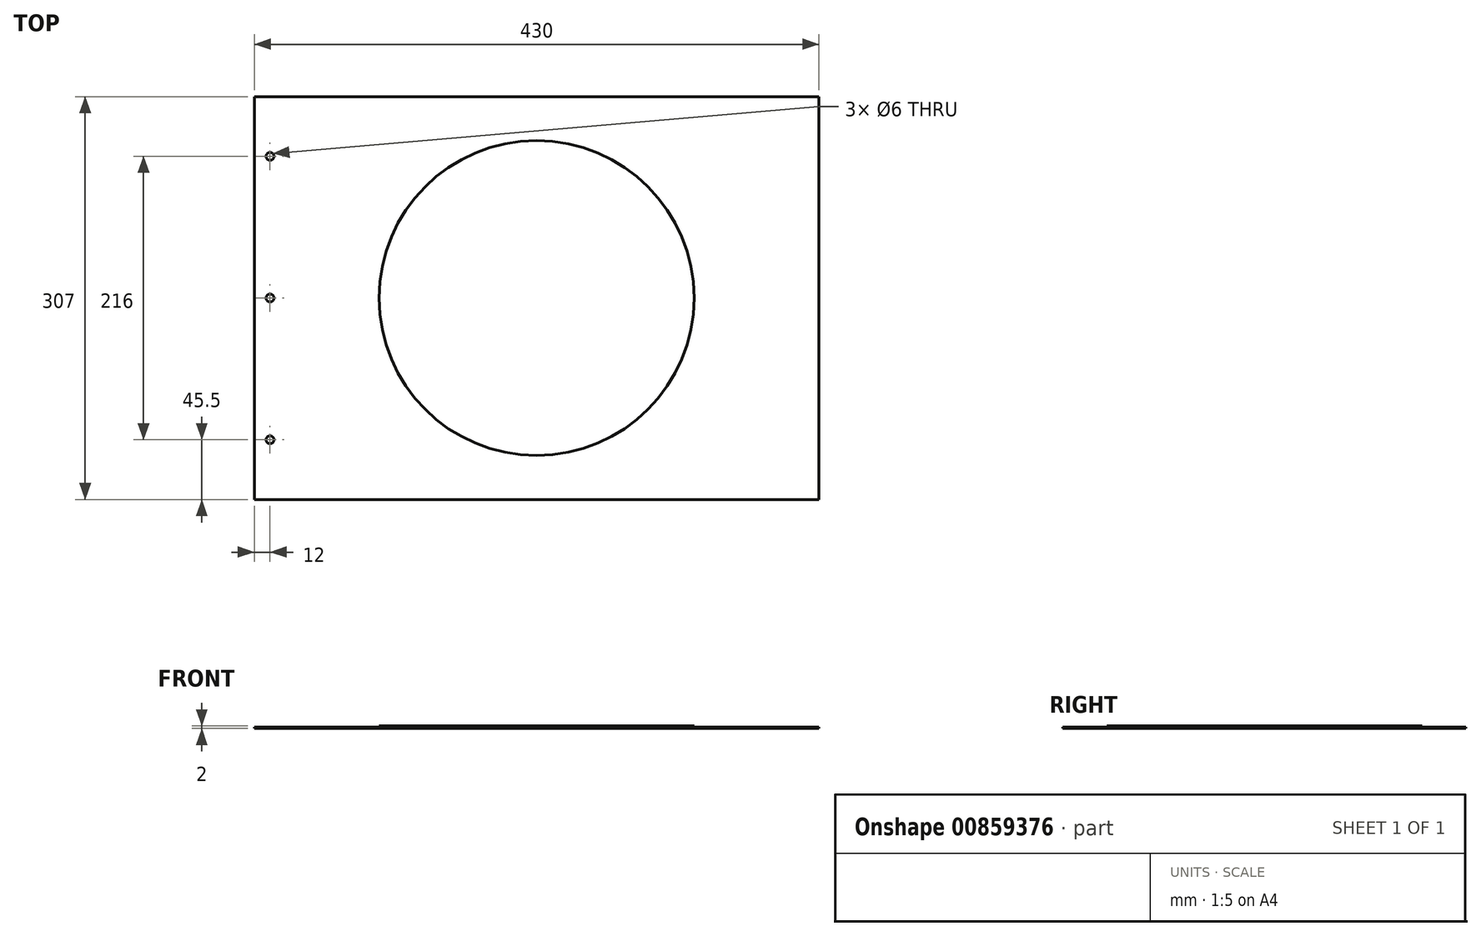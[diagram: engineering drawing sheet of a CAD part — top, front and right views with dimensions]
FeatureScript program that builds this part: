
annotation { "Feature Type Name" : "Feature", "Feature Type Description" : "" }
export const myFeature = defineFeature(function(context is Context, id is Id, definition is map)
    precondition{}
    {
        {
            var Q0;
            Q0=qCreatedBy(makeId("Top.planeOp"),FACE);
            var sketch = newSketch(context, id + "F0", { "sketchPlane" : qUnion([Q0])});
            skLineSegment(sketch, "E0.bottom", {"start": v(-215, 153.5) * mm, "end": v(215, 153.5) * mm});
            skLineSegment(sketch, "E0.top", {"start": v(-215, -153.5) * mm, "end": v(215, -153.5) * mm});
            skLineSegment(sketch, "E0.left", {"start": v(-215, 153.5) * mm, "end": v(-215, -153.5) * mm});
            skLineSegment(sketch, "E0.right", {"start": v(215, 153.5) * mm, "end": v(215, -153.5) * mm});
            skPoint(sketch, "E0.middle", {"position": v(0, 0) * mm});
            skLineSegment(sketch, "E1", {"start": v(-203, 153.5) * mm, "end": v(-203, -153.5) * mm, "construction": true});
            skCircle(sketch, "E2", {"center": v(-203, 108) * mm, "radius": 3 * mm});
            skCircle(sketch, "E3", {"center": v(-203, 0) * mm, "radius": 3 * mm});
            skCircle(sketch, "E4", {"center": v(-203, -108) * mm, "radius": 3 * mm});
            skCircle(sketch, "E5", {"center": v(0, 0) * mm, "radius": 120 * mm});
            skLineSegment(sketch, "E6", {"start": v(0, 0) * mm, "end": v(-120, 0) * mm});
            skLineSegment(sketch, "E7", {"start": v(0, 0) * mm, "end": v(0, 120) * mm});
            skLineSegment(sketch, "E8", {"start": v(0, 0) * mm, "end": v(120, 0) * mm});
            skLineSegment(sketch, "E9", {"start": v(0, 0) * mm, "end": v(0, -120) * mm});
            skSolve(sketch);
        }
        {
            var Q0;
            Q0=makeQuery(id+"F0.imprint","IMPRINT",FACE,{"disambiguationData":[TD([[makeQuery(id+"F0.imprint","IMPRINT",EDGE,{"derivedFrom":sQuery(id+"F0.wireOp",EDGE,"E0.bottom")}),-1.0]])]});
            extrude(context, id + "F1", {"entities" : qUnion([Q0]), "depth" : 1 * mm, "offsetDistance" : 25 * mm});
        }
        {
            var Q0;
            {var subQ0=sQuery(id+"F0.wireOp",EDGE,"E6");Q0=makeQuery(id+"F0.imprint","IMPRINT",FACE,{"disambiguationData":[TD([[makeQuery(id+"F0.imprint","IMPRINT",EDGE,{"derivedFrom":subQ0}),-1.0]])]});}
            var Q1;
            {var subQ0=sQuery(id+"F0.wireOp",EDGE,"E7");Q1=makeQuery(id+"F0.imprint","IMPRINT",FACE,{"disambiguationData":[TD([[makeQuery(id+"F0.imprint","IMPRINT",EDGE,{"derivedFrom":subQ0}),-1.0]])]});}
            var Q2;
            {var subQ0=sQuery(id+"F0.wireOp",EDGE,"E8");Q2=makeQuery(id+"F0.imprint","IMPRINT",FACE,{"disambiguationData":[TD([[makeQuery(id+"F0.imprint","IMPRINT",EDGE,{"derivedFrom":subQ0}),-1.0]])]});}
            var Q3;
            {var subQ0=sQuery(id+"F0.wireOp",EDGE,"E6");Q3=makeQuery(id+"F0.imprint","IMPRINT",FACE,{"disambiguationData":[TD([[makeQuery(id+"F0.imprint","IMPRINT",EDGE,{"derivedFrom":subQ0}),1.0]])]});}
            extrude(context, id + "F2", {"entities" : qUnion([Q0, Q1, Q2, Q3]), "operationType" : NewBodyOperationType.ADD, "depth" : 2 * mm, "offsetDistance" : 25 * mm});
        }
    });
